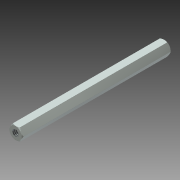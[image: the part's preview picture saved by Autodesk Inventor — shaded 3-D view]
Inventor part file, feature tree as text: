
AUTODESK INVENTOR PART (.ipt)
format: ipt  version: 2013 (Build 170138000, 138)  size: 117,248 bytes
history: native  units: mm (DEFAULTED — no unit token found)
features: sketch x4, hole x2, extrude x1, plane x1, revolve x1
ambient origin geometry x8: Origin, YZ Plane, XZ Plane, XY Plane, X Axis, Y Axis, Z Axis, Center Point
bodies: Solid1 (feature_tree)
feature tree (9):
  extrude  "Extrusion1"  Depth=76.2mm TaperAngle=0.0deg
  plane  "Work Plane1"
  revolve  "Revolution1"  [1 undecoded]
  hole  "Hole2"  [1 undecoded]
  hole  "Hole3"  [1 undecoded]
  sketch  "Sketch1"  dims[d0=6.35mm d1=76.2mm d2=0.0mm]
  sketch  "Sketch3"  dims[d4=-3.175mm d5=0.508mm]
  sketch  "Sketch5"  dims[d6=0.508mm d7=0.508mm]
  sketch  "Sketch6"  dims[d8=0.508mm d9=0.508mm d10=0.508mm d11=0.508mm d12=0.508mm d13=7.3152mm d14=0.0mm d15=76.2mm d16=0.0mm d17=90.0deg d25=3.302mm d26=12.7mm d27=9.525mm d28=6.35mm d29=14.3117mm d30=12.7mm d31=20.594885mm d32=3.302mm d33=12.7mm d34=9.525mm d35=6.35mm d36=14.3117mm d37=12.7mm d38=20.594885mm]
note: 3 required parameter values undecoded (feature->parameter linkage not recoverable at this tier; creation-order binding heuristic only, values carry confidence <= 0.55)